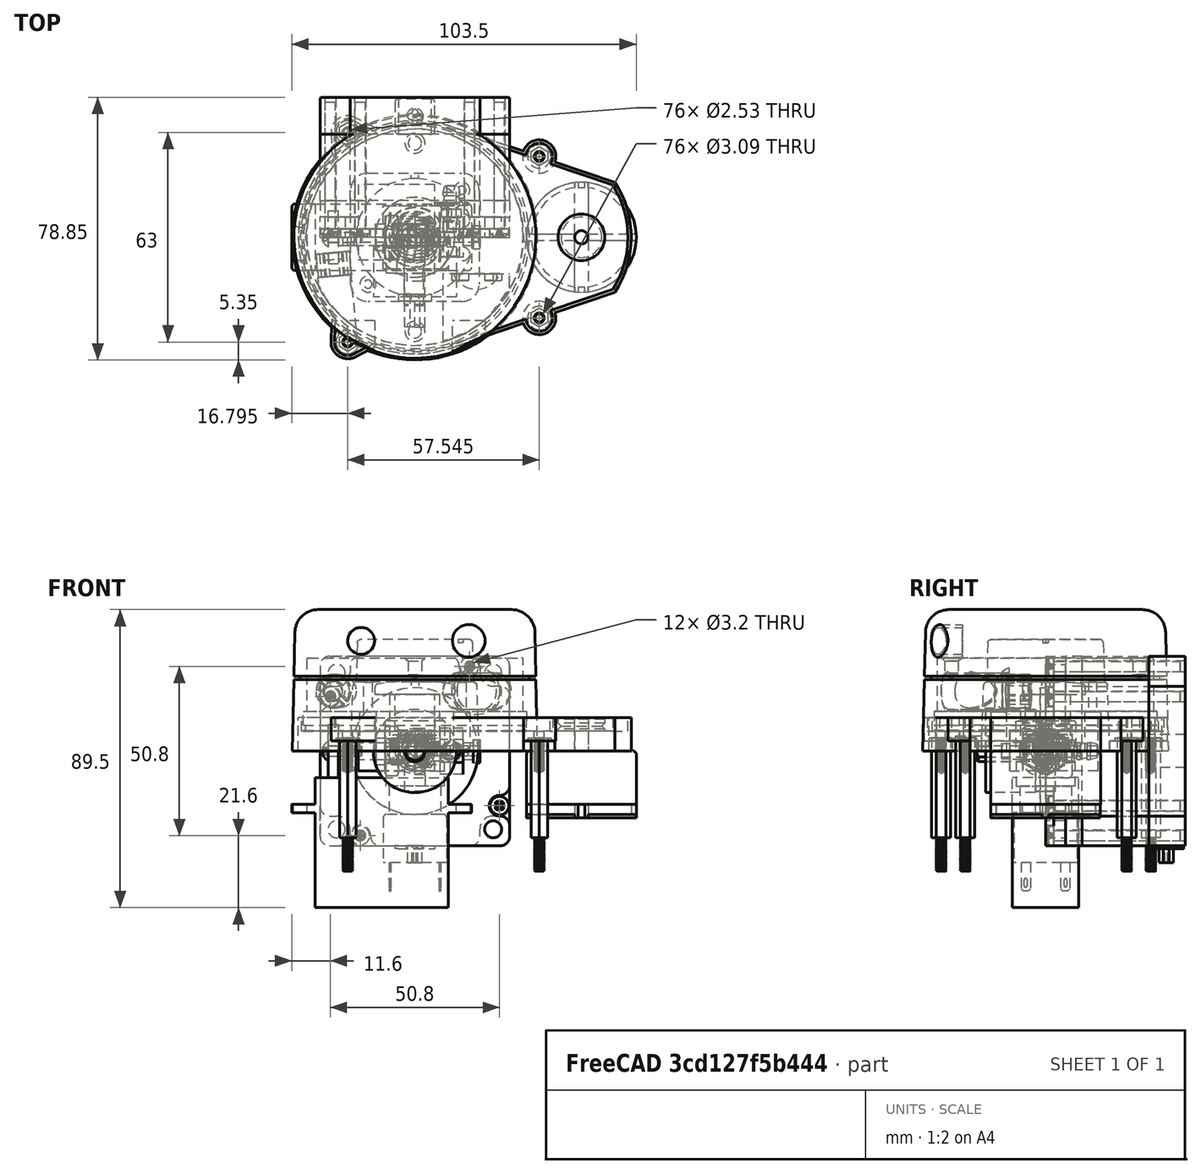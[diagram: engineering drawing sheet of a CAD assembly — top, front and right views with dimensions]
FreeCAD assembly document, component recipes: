
FREECAD ASSEMBLY — COMPONENT RECIPES ("generic-hardware")

This assembly document has 24 components, labeled P0..P23 below (a component is one placed body or linked part). 22 of them carry a construction recipe — the FreeCAD feature program that regenerates the part from scratch, quoted from this document or its linked companion documents; the rest are supplied as boundary geometry only. No exploded tour is included for this assembly.
NOTE — document 2 of 2 of this assembly tour. The two overview renders and the header above are repeated from document 1; the component sections below continue where the previous document stopped.
COMPONENT P19 — recipe-attached ("BAU-2195813", modeled in this document).
Construction recipe (the document's own serialized feature program — sketch geometry with constraints, then the solid features built on it; lengths are millimeters unless a unit is written):

FEATURE [Sketcher::SketchObject] Sketch171
  ArcFitTolerance = 0
  AttachmentSupport = -> [XY_Plane102]
  ExternalBSplineMaxDegree = 0
  ExternalBSplineTolerance = 0
  FixShape = 1
  FullyConstrained = true
  InternalTolerance = 1e-06
  InvalidShape = false
  MakeInternals = false
  MapMode = 5
  Support = -> [XY_Plane102]
  TreeRank = 111
  ValidateShape = false
  sketch-geometry (1):
    g0: Circle CenterX=0 CenterY=0 CenterZ=0 NormalX=0 NormalY=0 NormalZ=1 AngleXU=0 Radius=9
  constraints (2):
    c: Coincident(g0,g-1)
    c: Diameter(g0) = 18
FEATURE [PartDesign::Pad] Pad073
  AddSubType = 0
  AlongSketchNormal = false
  AutoTaperInnerAngle = false
  CheckUpToFaceLimits = true
  ClaimChildren = false
  Direction = (0,0,1)
  Fit = 0
  FitJoin = 0
  FixShape = 1
  InnerFit = 0
  InnerFitJoin = 0
  InvalidShape = false
  Length = 9
  Length2 = 100
  Linearize = true
  NewSolid = false
  Profile = -> Sketch171
  Refine = true
  Suppress = false
  TaperInnerAngle = 0
  TaperInnerAngleRev = 0
  TreeRank = 112
  Type = 0
  ValidateShape = false
  _ProfileBasedVersion = 1
FEATURE [PartDesign::Fillet] Fillet041
  AddSubType = 0
  Base = -> Pad073 [Edge3]
  BaseFeature = -> Pad073
  FixShape = 1
  InvalidShape = false
  NewSolid = false
  Radius = 0.4
  Refine = true
  SupportTransform = false
  Suppress = false
  TreeRank = 113
  UseAllEdges = false
  ValidateShape = false
FEATURE [Sketcher::SketchObject] Sketch172
  ArcFitTolerance = 0
  AttachmentSupport = -> [XZ_Plane102]
  ExternalBSplineMaxDegree = 0
  ExternalBSplineTolerance = 0
  FixShape = 1
  FullyConstrained = true
  InternalTolerance = 1e-06
  InvalidShape = false
  MakeInternals = false
  MapMode = 5
  Placement = pos=(0,0,0) rot=(1,0,0;1.5708rad)
  Support = -> [XZ_Plane102]
  TreeRank = 114
  ValidateShape = false
  sketch-geometry (8):
    g0: LineSegment StartX=0 StartY=-2.075e-13 StartZ=0 EndX=7.75 EndY=-2.075e-13 EndZ=0
    g1: LineSegment StartX=7.75 StartY=-2.075e-13 StartZ=0 EndX=7.75 EndY=-3 EndZ=0
    g2: LineSegment StartX=7.75 StartY=-3 StartZ=0 EndX=8.8 EndY=-3 EndZ=0
    g3: LineSegment StartX=8.8 StartY=-3 StartZ=0 EndX=8.8 EndY=-10.5 EndZ=0
    g4: LineSegment StartX=8.8 StartY=-10.5 StartZ=0 EndX=7.75 EndY=-10.5 EndZ=0
    g5: LineSegment StartX=7.75 StartY=-10.5 StartZ=0 EndX=7.75 EndY=-19 EndZ=0
    g6: LineSegment StartX=7.75 StartY=-19 StartZ=0 EndX=0 EndY=-19 EndZ=0
    g7: LineSegment StartX=0 StartY=-19 StartZ=0 EndX=0 EndY=-2.061e-13 EndZ=0
  constraints (23):
    c: Coincident(g-1,g0)
    c: Horizontal(g0)
    c: Coincident(g0,g1)
    c: Vertical(g1)
    c: Coincident(g1,g2)
    c: Horizontal(g2)
    c: Coincident(g2,g3)
    c: Vertical(g3)
    c: Coincident(g3,g4)
    c: Coincident(g4,g5)
    c: Vertical(g5)
    c: Coincident(g5,g6)
    c: PointOnObject(g6,g-2)
    c: Horizontal(g6)
    c: Coincident(g6,g7)
    c: Coincident(g7,g0)
    c: DistanceY(g1,g1) = 3
    c: DistanceX(g2) = 8.8
    c: DistanceX(g1) = 7.75
    c: PointOnObject(g5,g1)
    c: DistanceY(g3,g3) = 7.5
    c: Horizontal(g4)
    c: DistanceY(g7,g7) = 19
FEATURE [PartDesign::Revolution] Revolution014
  AddSubType = 0
  Angle = 360
  Axis = (0,2e-16,1)
  Base = (0,0,0)
  BaseFeature = -> Fillet041
  ClaimChildren = false
  Fit = 0
  FitJoin = 0
  FixShape = 1
  InnerFit = 0
  InnerFitJoin = 0
  InvalidShape = false
  Linearize = true
  NewSolid = false
  Profile = -> Sketch172
  ReferenceAxis = -> Sketch172 [V_Axis]
  Refine = true
  Reversed = true
  Suppress = false
  TreeRank = 115
  ValidateShape = false
  _ProfileBasedVersion = 1
FEATURE [PartDesign::Body] Body082  label="MainBody"
  AutoGroupSolids = false
  ClaimAllChildren = false
  ExportMode = 0
  FixShape = 1
  Group = -> [Sketch171,Pad073,Fillet041,Sketch172,Revolution014]
  InvalidShape = false
  Origin = -> Origin169
  SingleSolid = true
  Tip = -> Revolution014
  TreeRank = 110
  ValidateShape = false
  _ExportChildren = -> [Pad073,Fillet041,Revolution014]
  _GroupVersion = 1
FEATURE [Part::SubShapeBinder] Import002  label="Import002(Revolution014)"
  BindCopyOnChange = 0
  BindMode = 0
  ClaimChildren = false
  Context = -> Part036 [Body083.Import002.]
  EdgeTolerance = 1e-06
  FillStyle = 0
  FixShape = 1
  Fuse = false
  InvalidShape = false
  MakeFace = false
  MergeEdges = true
  OffsetFill = false
  OffsetIntersection = false
  OffsetJoinType = 0
  OffsetOpenResult = false
  Outline = false
  PartialLoad = false
  Relative = true
  SplitEdges = false
  Support = -> [Body082[Revolution014.]]
  TightBound = false
  TreeRank = 127
  ValidateShape = false
  _Version = 8
FEATURE [Sketcher::SketchObject] Sketch173
  ArcFitTolerance = 0
  AttachmentSupport = -> [Import002]
  ExternalBSplineMaxDegree = 0
  ExternalBSplineTolerance = 0
  FixShape = 1
  FullyConstrained = true
  InternalTolerance = 1e-06
  InvalidShape = false
  MakeInternals = false
  MapMode = 5
  Placement = pos=(0,-4.2e-15,-19) rot=(1,0,0;3.14159rad)
  Support = -> [Import002]
  TreeRank = 126
  ValidateShape = false
  sketch-geometry (5):
    g0: LineSegment StartX=9.5 StartY=9.5 StartZ=0 EndX=-9.5 EndY=9.5 EndZ=0
    g1: LineSegment StartX=-9.5 StartY=9.5 StartZ=0 EndX=-9.5 EndY=-9.5 EndZ=0
    g2: LineSegment StartX=-9.5 StartY=-9.5 StartZ=0 EndX=9.5 EndY=-9.5 EndZ=0
    g3: LineSegment StartX=9.5 StartY=-9.5 StartZ=0 EndX=9.5 EndY=9.5 EndZ=0
    g4: Circle [constr] CenterX=-1.2948e-12 CenterY=-4.7939e-12 CenterZ=0 NormalX=0 NormalY=0 NormalZ=1 AngleXU=0 Radius=13.435
  constraints (14):
    c: Coincident(g0,g1)
    c: Coincident(g1,g2)
    c: Coincident(g2,g3)
    c: Coincident(g3,g0)
    c: Equal(g0,g1)
    c: Equal(g0,g2)
    c: Equal(g0,g3)
    c: PointOnObject(g0,g4)
    c: PointOnObject(g1,g4)
    c: PointOnObject(g2,g4)
    c: PointOnObject(g3,g4)
    c: Coincident(g4,g-1)
    c: Horizontal(g0)
    c: DistanceX(g0,g0) = 19
FEATURE [PartDesign::Pad] Pad074
  AddSubType = 0
  AlongSketchNormal = false
  AutoTaperInnerAngle = false
  CheckUpToFaceLimits = true
  ClaimChildren = false
  Direction = (0,-2e-16,-1)
  Fit = 0
  FitJoin = 0
  FixShape = 1
  InnerFit = 0
  InnerFitJoin = 0
  InvalidShape = false
  Length = 14.5
  Length2 = 100
  Linearize = true
  NewSolid = false
  Profile = -> Sketch173
  Refine = true
  Suppress = false
  TaperInnerAngle = 0
  TaperInnerAngleRev = 0
  TreeRank = 128
  Type = 0
  ValidateShape = false
  _ProfileBasedVersion = 1
FEATURE [PartDesign::Fillet] Fillet042
  AddSubType = 0
  Base = -> Pad074 [Edge11,Edge6]
  BaseFeature = -> Pad074
  FixShape = 1
  InvalidShape = false
  NewSolid = false
  Radius = 1
  Refine = true
  SupportTransform = false
  Suppress = false
  TreeRank = 129
  UseAllEdges = false
  ValidateShape = false
FEATURE [PartDesign::Body] Body083  label="ElectronicBody"
  AutoGroupSolids = false
  ClaimAllChildren = false
  ExportMode = 0
  FixShape = 1
  Group = -> [Sketch173,Import002,Pad074,Fillet042]
  InvalidShape = false
  Origin = -> Origin170
  SingleSolid = true
  Tip = -> Fillet042
  TreeRank = 125
  ValidateShape = false
  _ExportChildren = -> [Import002,Pad074,Fillet042]
  _GroupVersion = 1
FEATURE [Part::SubShapeBinder] Import003  label="Import003(Fillet042)"
  BindCopyOnChange = 0
  BindMode = 0
  ClaimChildren = false
  Context = -> Part036 [Body084.Import003.]
  EdgeTolerance = 1e-06
  FillStyle = 0
  FixShape = 1
  Fuse = false
  InvalidShape = false
  MakeFace = false
  MergeEdges = true
  OffsetFill = false
  OffsetIntersection = false
  OffsetJoinType = 0
  OffsetOpenResult = false
  Outline = false
  PartialLoad = false
  Relative = true
  SplitEdges = false
  Support = -> [Body083[Fillet042.]]
  TightBound = false
  TreeRank = 141
  ValidateShape = false
  _Version = 8
FEATURE [Sketcher::SketchObject] Sketch174
  ArcFitTolerance = 0
  AttachmentSupport = -> [Import003]
  ExternalBSplineMaxDegree = 0
  ExternalBSplineTolerance = 0
  FixShape = 1
  FullyConstrained = true
  InternalTolerance = 1e-06
  InvalidShape = false
  MakeInternals = false
  MapMode = 5
  Placement = pos=(0,-1.25e-14,-33.5) rot=(1,0,0;3.14159rad)
  Support = -> [Import003]
  TreeRank = 140
  ValidateShape = false
  sketch-geometry (16):
    g0: LineSegment StartX=-7.75 StartY=7.3 StartZ=0 EndX=-7.25 EndY=7.3 EndZ=0
    g1: LineSegment StartX=-7.25 StartY=7.3 StartZ=0 EndX=-7.25 EndY=4.5 EndZ=0
    g2: LineSegment StartX=-7.25 StartY=4.5 StartZ=0 EndX=-7.75 EndY=4.5 EndZ=0
    g3: LineSegment StartX=-7.75 StartY=4.5 StartZ=0 EndX=-7.75 EndY=7.3 EndZ=0
    g4: LineSegment StartX=7.25 StartY=7.3 StartZ=0 EndX=7.75 EndY=7.3 EndZ=0
    g5: LineSegment StartX=7.75 StartY=7.3 StartZ=0 EndX=7.75 EndY=4.5 EndZ=0
    g6: LineSegment StartX=7.75 StartY=4.5 StartZ=0 EndX=7.25 EndY=4.5 EndZ=0
    g7: LineSegment StartX=7.25 StartY=4.5 StartZ=0 EndX=7.25 EndY=7.3 EndZ=0
    g8: LineSegment StartX=7.25 StartY=-4.5 StartZ=0 EndX=7.75 EndY=-4.5 EndZ=0
    g9: LineSegment StartX=7.75 StartY=-4.5 StartZ=0 EndX=7.75 EndY=-7.3 EndZ=0
    g10: LineSegment StartX=7.75 StartY=-7.3 StartZ=0 EndX=7.25 EndY=-7.3 EndZ=0
    g11: LineSegment StartX=7.25 StartY=-7.3 StartZ=0 EndX=7.25 EndY=-4.5 EndZ=0
    g12: LineSegment StartX=-7.75 StartY=-4.5 StartZ=0 EndX=-7.25 EndY=-4.5 EndZ=0
    g13: LineSegment StartX=-7.25 StartY=-4.5 StartZ=0 EndX=-7.25 EndY=-7.3 EndZ=0
    g14: LineSegment StartX=-7.25 StartY=-7.3 StartZ=0 EndX=-7.75 EndY=-7.3 EndZ=0
    g15: LineSegment StartX=-7.75 StartY=-7.3 StartZ=0 EndX=-7.75 EndY=-4.5 EndZ=0
  constraints (46):
    c: Coincident(g0,g1)
    c: Coincident(g1,g2)
    c: Coincident(g2,g3)
    c: Coincident(g3,g0)
    c: Horizontal(g0)
    c: Horizontal(g2)
    c: Vertical(g1)
    c: Vertical(g3)
    c: DistanceX(g1,g-1) = 7.25
    c: DistanceX(g0,g0) = 0.5
    c: DistanceY(g3,g3) = 2.8
    c: DistanceY(g2) = 4.5
    c: Coincident(g4,g5)
    c: Coincident(g5,g6)
    c: Coincident(g6,g7)
    c: Coincident(g7,g4)
    c: Horizontal(g4)
    c: Horizontal(g6)
    c: Vertical(g5)
    c: Vertical(g7)
    c: Coincident(g8,g9)
    c: Coincident(g9,g10)
    c: Coincident(g10,g11)
    c: Coincident(g11,g8)
    c: Horizontal(g8)
    c: Horizontal(g10)
    c: Vertical(g9)
    c: Vertical(g11)
    c: Coincident(g12,g13)
    c: Coincident(g13,g14)
    c: Coincident(g14,g15)
    c: Coincident(g15,g12)
    c: Horizontal(g12)
    c: Horizontal(g14)
    c: Vertical(g13)
    c: Vertical(g15)
    c: Equal(g12,g8)
    c: Equal(g8,g6)
    c: Equal(g6,g2)
    c: Equal(g1,g7)
    c: Equal(g7,g11)
    c: Equal(g11,g13)
    c: Horizontal(g13,g10)
    c: Vertical(g8,g5)
    c: Symmetric(g0,g4,g-2)
    c: Symmetric(g12,g1,g-1)
FEATURE [PartDesign::Pad] Pad075
  AddSubType = 0
  AlongSketchNormal = false
  AutoTaperInnerAngle = false
  CheckUpToFaceLimits = true
  ClaimChildren = false
  Direction = (0,-4e-16,-1)
  Fit = 0
  FitJoin = 0
  FixShape = 1
  InnerFit = 0
  InnerFitJoin = 0
  InvalidShape = false
  Length = 8.5
  Length2 = 100
  Linearize = true
  NewSolid = false
  Profile = -> Sketch174
  Refine = true
  Suppress = false
  TaperInnerAngle = 0
  TaperInnerAngleRev = 0
  TreeRank = 142
  Type = 0
  ValidateShape = false
  _ProfileBasedVersion = 1
FEATURE [PartDesign::Chamfer] Chamfer045
  AddSubType = 0
  Angle = 45
  Base = -> Pad075 [Edge46,Edge40,Edge34,Edge28,Edge16,Edge22,Edge10,Edge4]
  BaseFeature = -> Pad075
  ChamferType = 0
  FixShape = 1
  FlipDirection = false
  InvalidShape = false
  NewSolid = false
  Refine = true
  Size = 0.6
  Size2 = 1
  SupportTransform = false
  Suppress = false
  TreeRank = 143
  UseAllEdges = false
  ValidateShape = false
FEATURE [Sketcher::SketchObject] Sketch175
  ArcFitTolerance = 0
  AttachmentSupport = -> [YZ_Plane104]
  ExternalBSplineMaxDegree = 0
  ExternalBSplineTolerance = 0
  FixShape = 1
  FullyConstrained = false
  InternalTolerance = 1e-06
  InvalidShape = false
  MakeInternals = false
  MapMode = 5
  Placement = pos=(0,0,0) rot=(0.57735,0.57735,0.57735;2.0944rad)
  Support = -> [YZ_Plane104]
  TreeRank = 144
  ValidateShape = false
  sketch-geometry (8):
    g0: ArcOfCircle CenterX=-6 CenterY=-38.7066 CenterZ=0 NormalX=0 NormalY=0 NormalZ=1 AngleXU=0 Radius=0.456793 StartAngle=1.3e-15 EndAngle=3.14159
    g1: ArcOfCircle CenterX=-6 CenterY=-40.4194 CenterZ=0 NormalX=0 NormalY=0 NormalZ=1 AngleXU=0 Radius=0.456793 StartAngle=3.14159 EndAngle=6.28319
    g2: LineSegment StartX=-6.45679 StartY=-38.7066 StartZ=0 EndX=-6.45679 EndY=-40.4194 EndZ=0
    g3: LineSegment StartX=-5.54321 StartY=-40.4194 StartZ=0 EndX=-5.54321 EndY=-38.7066 EndZ=0
    g4: ArcOfCircle CenterX=6 CenterY=-38.7066 CenterZ=0 NormalX=0 NormalY=0 NormalZ=1 AngleXU=0 Radius=0.417287 StartAngle=-5.3e-15 EndAngle=3.14159
    g5: ArcOfCircle CenterX=6 CenterY=-40.4194 CenterZ=0 NormalX=0 NormalY=0 NormalZ=1 AngleXU=0 Radius=0.417287 StartAngle=3.14159 EndAngle=6.28319
    g6: LineSegment StartX=5.58271 StartY=-38.7066 StartZ=0 EndX=5.58271 EndY=-40.4194 EndZ=0
    g7: LineSegment StartX=6.41729 StartY=-40.4194 StartZ=0 EndX=6.41729 EndY=-38.7066 EndZ=0
  constraints (14):
    c: Tangent(g0,g2) = -1.5708
    c: Tangent(g2,g1) = -1.5708
    c: Tangent(g1,g3) = -1.5708
    c: Tangent(g3,g0) = -1.5708
    c: Equal(g0,g1)
    c: Tangent(g4,g6) = -1.5708
    c: Tangent(g6,g5) = -1.5708
    c: Tangent(g5,g7) = -1.5708
    c: Tangent(g7,g4) = -1.5708
    c: Equal(g4,g5)
    c: Symmetric(g4,g0,g-2)
    c: Symmetric(g5,g1,g-2)
    c: Vertical(g1,g0)
    c: DistanceX(g0) = -6
FEATURE [PartDesign::Pocket] Pocket054
  AddSubType = 1
  AutoTaperInnerAngle = false
  BaseFeature = -> Chamfer045
  CheckUpToFaceLimits = true
  ClaimChildren = false
  Direction = (1,1,1)
  Fit = 0
  FitJoin = 0
  FixShape = 1
  InnerFit = 0
  InnerFitJoin = 0
  InvalidShape = false
  Length = 5
  Length2 = 100
  Linearize = true
  Midplane = true
  NewSolid = false
  Profile = -> Sketch175
  Refine = true
  Suppress = false
  TaperInnerAngle = 0
  TaperInnerAngleRev = 0
  TreeRank = 145
  Type = 1
  ValidateShape = false
  _ProfileBasedVersion = 1
  _Version = 1
FEATURE [PartDesign::Body] Body084  label="ElectronicPins"
  AutoGroupSolids = false
  ClaimAllChildren = false
  ExportMode = 0
  FixShape = 1
  Group = -> [Sketch174,Import003,Pad075,Chamfer045,Sketch175,Pocket054]
  InvalidShape = false
  Origin = -> Origin171
  Tip = -> Pocket054
  TreeRank = 139
  ValidateShape = false
  _ExportChildren = -> [Import003,Pad075,Chamfer045,Pocket054]
  _GroupVersion = 1
FEATURE [Sketcher::SketchObject] Sketch176
  ArcFitTolerance = 0
  AttachmentSupport = -> [YZ_Plane105]
  ExternalBSplineMaxDegree = 0
  ExternalBSplineTolerance = 0
  FixShape = 1
  FullyConstrained = true
  InternalTolerance = 1e-06
  InvalidShape = false
  MakeInternals = false
  MapMode = 5
  Placement = pos=(0,0,0) rot=(0.57735,0.57735,0.57735;2.0944rad)
  Support = -> [YZ_Plane105]
  TreeRank = 156
  ValidateShape = false
  sketch-geometry (12):
    g0: LineSegment StartX=-7.5 StartY=0 StartZ=0 EndX=-7.5 EndY=17 EndZ=0
    g1: LineSegment StartX=-7.5 StartY=17 StartZ=0 EndX=-12 EndY=17 EndZ=0
    g2: LineSegment StartX=-12 StartY=17 StartZ=0 EndX=-12 EndY=20 EndZ=0
    g3: LineSegment [constr] StartX=-7.5 StartY=0 StartZ=0 EndX=7.5 EndY=0 EndZ=0
    g4: LineSegment [constr] StartX=7.5 StartY=0 StartZ=0 EndX=7.5 EndY=17 EndZ=0
    g5: LineSegment [constr] StartX=7.5 StartY=17 StartZ=0 EndX=12 EndY=17 EndZ=0
    g6: LineSegment [constr] StartX=12 StartY=17 StartZ=0 EndX=12 EndY=20 EndZ=0
    g7: ArcOfCircle [constr] CenterX=-1.51e-14 CenterY=-51.5 CenterZ=0 NormalX=0 NormalY=0 NormalZ=1 AngleXU=0 Radius=72.5 StartAngle=1.40451 EndAngle=1.73708
    g8: GeomPoint [constr] X=4.5e-15 Y=21 Z=0
    g9: LineSegment StartX=0 StartY=0 StartZ=0 EndX=4.5e-15 EndY=21 EndZ=0
    g10: LineSegment StartX=-7.5 StartY=0 StartZ=0 EndX=0 EndY=0 EndZ=0
    g11: ArcOfCircle CenterX=-1.51e-14 CenterY=-51.5 CenterZ=0 NormalX=0 NormalY=0 NormalZ=1 AngleXU=0 Radius=72.5 StartAngle=1.5708 EndAngle=1.73708
  constraints (31):
    c: PointOnObject(g0,g-1)
    c: Vertical(g0)
    c: Coincident(g0,g1)
    c: Horizontal(g1)
    c: Coincident(g1,g2)
    c: Coincident(g0,g3)
    c: Coincident(g3,g4)
    c: Vertical(g4)
    c: Coincident(g4,g5)
    c: Horizontal(g5)
    c: Coincident(g5,g6)
    c: Vertical(g6)
    c: Vertical(g2)
    c: Equal(g6,g2)
    c: Symmetric(g0,g3,g-1)
    c: Symmetric(g6,g2,g-2)
    c: DistanceX(g0,g4) = 15
    c: DistanceY(g4) = 17
    c: DistanceY(g2,g2) = 3
    c: DistanceX(g1,g5) = 24
    c: Coincident(g7,g2)
    c: Coincident(g7,g6)
    c: PointOnObject(g8,g-2)
    c: Coincident(g9,g-1)
    c: Coincident(g9,g8)
    c: Coincident(g10,g0)
    c: Coincident(g10,g9)
    c: Coincident(g11,g7)
    c: Coincident(g11,g9)
    c: Coincident(g11,g2)
    c: DistanceY(g9) = 21
FEATURE [PartDesign::Revolution] Revolution015
  AddSubType = 0
  Angle = 360
  Axis = (-2e-16,3e-16,1)
  Base = (0,0,0)
  ClaimChildren = false
  Fit = 0
  FitJoin = 0
  FixShape = 1
  InnerFit = 0
  InnerFitJoin = 0
  InvalidShape = false
  Linearize = true
  NewSolid = false
  Placement = pos=(0,0,0) rot=(0.57735,0.57735,0.57735;2.0944rad)
  Profile = -> Sketch176
  ReferenceAxis = -> Sketch176 [V_Axis]
  Refine = true
  Suppress = false
  TreeRank = 157
  ValidateShape = false
  _ProfileBasedVersion = 1
FEATURE [PartDesign::Fillet] Fillet043
  AddSubType = 0
  Base = -> Revolution015 [Edge5]
  BaseFeature = -> Revolution015
  FixShape = 1
  InvalidShape = false
  NewSolid = false
  Placement = pos=(0,0,0) rot=(0.57735,0.57735,0.57735;2.0944rad)
  Radius = 1
  Refine = true
  SupportTransform = false
  Suppress = false
  TreeRank = 158
  UseAllEdges = false
  ValidateShape = false
FEATURE [PartDesign::Body] Body085  label="ButtonCaps"
  AutoGroupSolids = false
  ClaimAllChildren = false
  ExportMode = 0
  FixShape = 1
  Group = -> [Sketch176,Revolution015,Fillet043]
  InvalidShape = false
  Origin = -> Origin172
  SingleSolid = true
  Tip = -> Fillet043
  TreeRank = 155
  ValidateShape = false
  _ExportChildren = -> [Revolution015,Fillet043]
  _GroupVersion = 1
COMPONENT P20 — geometry summary ("ConnecteurPneu-Ressort"; no construction recipe available for this part):
  bounding box: 47.1 x 23.5 x 16.0 mm
  tessellated surface: 18,782 triangles
  volume: 3419 mm^3 (19% of its bounding box)
  symmetry: mirror-symmetric across its z mid-plane
COMPONENT P21 — recipe-attached ("623ZZ", modeled in this document).
Construction recipe (the document's own serialized feature program — sketch geometry with constraints, then the solid features built on it; lengths are millimeters unless a unit is written):

FEATURE [Sketcher::SketchObject] Sketch202
  ArcFitTolerance = 1e-06
  AttachmentSupport = -> [XY_Plane117]
  ExternalBSplineMaxDegree = 5
  ExternalBSplineTolerance = 0.0001
  FixShape = 1
  FullyConstrained = true
  InternalTolerance = 1e-06
  InvalidShape = false
  MakeInternals = false
  MapMode = 5
  Support = -> [XY_Plane117]
  TreeRank = 345
  ValidateShape = false
  sketch-geometry (12):
    g0: LineSegment StartX=0 StartY=1.5 StartZ=0 EndX=4 EndY=1.5 EndZ=0
    g1: LineSegment StartX=4 StartY=1.5 StartZ=0 EndX=4 EndY=2.5 EndZ=0
    g2: LineSegment StartX=4 StartY=2.5 StartZ=0 EndX=3.5 EndY=2.5 EndZ=0
    g3: LineSegment StartX=3.5 StartY=2.5 StartZ=0 EndX=3.5 EndY=4 EndZ=0
    g4: LineSegment StartX=3.5 StartY=4 StartZ=0 EndX=4 EndY=4 EndZ=0
    g5: LineSegment StartX=4 StartY=4 StartZ=0 EndX=4 EndY=5 EndZ=0
    g6: LineSegment StartX=4 StartY=5 StartZ=0 EndX=0 EndY=5 EndZ=0
    g7: LineSegment StartX=0 StartY=5 StartZ=0 EndX=0 EndY=4 EndZ=0
    g8: LineSegment StartX=0 StartY=4 StartZ=0 EndX=0.5 EndY=4 EndZ=0
    g9: LineSegment StartX=0.5 StartY=4 StartZ=0 EndX=0.5 EndY=2.5 EndZ=0
    g10: LineSegment StartX=0.5 StartY=2.5 StartZ=0 EndX=0 EndY=2.5 EndZ=0
    g11: LineSegment StartX=0 StartY=2.5 StartZ=0 EndX=0 EndY=1.5 EndZ=0
  constraints (36):
    c: PointOnObject(g0,g-2)
    c: Horizontal(g0)
    c: Coincident(g1,g0)
    c: Vertical(g1)
    c: Coincident(g1,g2)
    c: Horizontal(g2)
    c: Coincident(g2,g3)
    c: Vertical(g3)
    c: Coincident(g3,g4)
    c: Horizontal(g4)
    c: Coincident(g4,g5)
    c: Vertical(g5)
    c: Coincident(g5,g6)
    c: PointOnObject(g6,g-2)
    c: Horizontal(g6)
    c: Coincident(g6,g7)
    c: PointOnObject(g7,g-2)
    c: Coincident(g7,g8)
    c: Horizontal(g8)
    c: Coincident(g8,g9)
    c: Vertical(g9)
    c: Coincident(g9,g10)
    c: PointOnObject(g10,g-2)
    c: Horizontal(g10)
    c: Coincident(g10,g11)
    c: Coincident(g11,g0)
    c: Equal(g4,g8)
    c: Equal(g10,g2)
    c: DistanceY(g-1,g0) = 1.5
    c: PointOnObject(g9,g2)
    c: PointOnObject(g8,g4)
    c: DistanceY(g-1,g6) = 5
    c: DistanceY(g-1,g10) = 2.5
    c: DistanceY(g-1,g7) = 4
    c: DistanceX(g6,g6) = 4
    c: DistanceX(g8,g3) = 3
FEATURE [PartDesign::Revolution] Revolution018
  AddSubType = 0
  Angle = 360
  Axis = (1,0,0)
  Base = (0,0,0)
  ClaimChildren = false
  Fit = 0
  FitJoin = 0
  FixShape = 1
  InnerFit = 0
  InnerFitJoin = 0
  InvalidShape = false
  Linearize = true
  NewSolid = false
  Profile = -> Sketch202
  ReferenceAxis = -> Sketch202 [H_Axis]
  Refine = true
  Suppress = false
  TreeRank = 346
  ValidateShape = false
  _ProfileBasedVersion = 1
FEATURE [PartDesign::Body] Body097
  AutoGroupSolids = false
  ClaimAllChildren = false
  ExportMode = 0
  FixShape = 1
  Group = -> [Sketch202,Revolution018]
  InvalidShape = false
  Origin = -> Origin188
  SingleSolid = true
  Tip = -> Revolution018
  TreeRank = 344
  ValidateShape = false
  _ExportChildren = -> [Revolution018]
  _GroupVersion = 1
FEATURE [Sketcher::SketchObject] Sketch203
  ArcFitTolerance = 1e-06
  AttachmentSupport = -> [XY_Plane118]
  ExternalBSplineMaxDegree = 5
  ExternalBSplineTolerance = 0.0001
  FixShape = 1
  FullyConstrained = true
  InternalTolerance = 1e-06
  InvalidShape = false
  MakeInternals = false
  MapMode = 5
  Support = -> [XY_Plane118]
  TreeRank = 357
  ValidateShape = false
  sketch-geometry (4):
    g0: LineSegment StartX=0.1 StartY=4 StartZ=0 EndX=3.9 EndY=4 EndZ=0
    g1: LineSegment StartX=3.9 StartY=4 StartZ=0 EndX=3.9 EndY=2.5 EndZ=0
    g2: LineSegment StartX=3.9 StartY=2.5 StartZ=0 EndX=0.1 EndY=2.5 EndZ=0
    g3: LineSegment StartX=0.1 StartY=2.5 StartZ=0 EndX=0.1 EndY=4 EndZ=0
  constraints (12):
    c: Coincident(g0,g1)
    c: Coincident(g1,g2)
    c: Coincident(g2,g3)
    c: Coincident(g3,g0)
    c: Horizontal(g0)
    c: Horizontal(g2)
    c: Vertical(g1)
    c: Vertical(g3)
    c: DistanceY(g-1,g2) = 2.5
    c: DistanceY(g-1,g0) = 4
    c: DistanceX(g0,g0) = 3.8
    c: DistanceX(g-1,g2) = 0.1
FEATURE [PartDesign::Revolution] Revolution019
  AddSubType = 0
  Angle = 360
  Axis = (1,0,0)
  Base = (0,0,0)
  ClaimChildren = false
  Fit = 0
  FitJoin = 0
  FixShape = 1
  InnerFit = 0
  InnerFitJoin = 0
  InvalidShape = false
  Linearize = true
  NewSolid = false
  Profile = -> Sketch203
  ReferenceAxis = -> Sketch203 [H_Axis]
  Refine = true
  Suppress = false
  TreeRank = 358
  ValidateShape = false
  _ProfileBasedVersion = 1
FEATURE [PartDesign::Body] Body098
  AutoGroupSolids = false
  ClaimAllChildren = false
  ExportMode = 0
  FixShape = 1
  Group = -> [Sketch203,Revolution019]
  InvalidShape = false
  Origin = -> Origin189
  SingleSolid = true
  Tip = -> Revolution019
  TreeRank = 356
  ValidateShape = false
  _ExportChildren = -> [Revolution019]
  _GroupVersion = 1
COMPONENT P22 — recipe-attached ("V623ZZ", modeled in this document).
Construction recipe (the document's own serialized feature program — sketch geometry with constraints, then the solid features built on it; lengths are millimeters unless a unit is written):

FEATURE [Sketcher::SketchObject] Sketch204
  ArcFitTolerance = 1e-06
  AttachmentSupport = -> [XY_Plane121]
  ExternalBSplineMaxDegree = 5
  ExternalBSplineTolerance = 0.0001
  FixShape = 1
  FullyConstrained = true
  InternalTolerance = 1e-06
  InvalidShape = false
  MakeInternals = false
  MapMode = 5
  Support = -> [XY_Plane121]
  TreeRank = 396
  ValidateShape = false
  sketch-geometry (7):
    g0: LineSegment StartX=4 StartY=0 StartZ=0 EndX=4 EndY=4 EndZ=0
    g1: LineSegment StartX=4 StartY=4 StartZ=0 EndX=6 EndY=4 EndZ=0
    g2: LineSegment StartX=6 StartY=4 StartZ=0 EndX=6 EndY=3.25 EndZ=0
    g3: LineSegment StartX=6 StartY=3.25 StartZ=0 EndX=4.85 EndY=2 EndZ=0
    g4: LineSegment StartX=4.85 StartY=2 StartZ=0 EndX=6 EndY=0.75 EndZ=0
    g5: LineSegment StartX=6 StartY=0.75 StartZ=0 EndX=6 EndY=0 EndZ=0
    g6: LineSegment StartX=6 StartY=0 StartZ=0 EndX=4 EndY=0 EndZ=0
  constraints (21):
    c: PointOnObject(g0,g-1)
    c: Vertical(g0)
    c: Coincident(g0,g1)
    c: Horizontal(g1)
    c: Coincident(g1,g2)
    c: Vertical(g2)
    c: Coincident(g2,g3)
    c: Coincident(g3,g4)
    c: Coincident(g4,g5)
    c: PointOnObject(g5,g-1)
    c: Vertical(g5)
    c: Coincident(g5,g6)
    c: Coincident(g6,g0)
    c: DistanceX(g-1,g0) = 4
    c: Equal(g3,g4)
    c: Equal(g1,g6)
    c: Equal(g5,g2)
    c: DistanceX(g-1,g5) = 6
    c: DistanceX(g-1,g3) = 4.85
    c: DistanceY(g0,g0) = 4
    c: DistanceY(g4,g2) = 2.5
FEATURE [PartDesign::Revolution] Revolution020
  AddSubType = 0
  Angle = 360
  Axis = (0,1,0)
  Base = (0,0,0)
  ClaimChildren = false
  Fit = 0
  FitJoin = 0
  FixShape = 1
  InnerFit = 0
  InnerFitJoin = 0
  InvalidShape = false
  Linearize = true
  NewSolid = false
  Profile = -> Sketch204
  ReferenceAxis = -> Sketch204 [V_Axis]
  Refine = true
  Reversed = true
  Suppress = false
  TreeRank = 397
  ValidateShape = false
  _ProfileBasedVersion = 1
FEATURE [PartDesign::Body] Body101  label="V623ZZ-extern"
  AutoGroupSolids = false
  ClaimAllChildren = false
  ExportMode = 0
  FixShape = 1
  Group = -> [Sketch204,Revolution020]
  InvalidShape = false
  Origin = -> Origin194
  SingleSolid = true
  Tip = -> Revolution020
  TreeRank = 395
  ValidateShape = false
  _ExportChildren = -> [Revolution020]
  _GroupVersion = 1
FEATURE [Sketcher::SketchObject] Sketch205
  ArcFitTolerance = 1e-06
  AttachmentSupport = -> [YZ_Plane120]
  ExternalBSplineMaxDegree = 5
  ExternalBSplineTolerance = 0.0001
  FixShape = 1
  FullyConstrained = true
  InternalTolerance = 1e-06
  InvalidShape = false
  MakeInternals = false
  MapMode = 5
  Placement = pos=(0,0,0) rot=(0.57735,0.57735,0.57735;2.0944rad)
  Support = -> [YZ_Plane120]
  TreeRank = 398
  ValidateShape = false
  sketch-geometry (8):
    g0: LineSegment StartX=0.2 StartY=4 StartZ=0 EndX=0.2 EndY=2.1 EndZ=0
    g1: LineSegment StartX=0.2 StartY=2.1 StartZ=0 EndX=0 EndY=2.1 EndZ=0
    g2: LineSegment StartX=0 StartY=2.1 StartZ=0 EndX=0 EndY=1.5 EndZ=0
    g3: LineSegment StartX=0 StartY=1.5 StartZ=0 EndX=4 EndY=1.5 EndZ=0
    g4: LineSegment StartX=4 StartY=1.5 StartZ=0 EndX=4 EndY=2.1 EndZ=0
    g5: LineSegment StartX=4 StartY=2.1 StartZ=0 EndX=3.8 EndY=2.1 EndZ=0
    g6: LineSegment StartX=3.8 StartY=2.1 StartZ=0 EndX=3.8 EndY=4 EndZ=0
    g7: LineSegment StartX=3.8 StartY=4 StartZ=0 EndX=0.2 EndY=4 EndZ=0
  constraints (24):
    c: Vertical(g0)
    c: Coincident(g0,g1)
    c: PointOnObject(g1,g-2)
    c: Horizontal(g1)
    c: Coincident(g1,g2)
    c: PointOnObject(g2,g-2)
    c: Coincident(g2,g3)
    c: Horizontal(g3)
    c: Coincident(g3,g4)
    c: Coincident(g4,g5)
    c: Horizontal(g5)
    c: Coincident(g5,g6)
    c: Vertical(g6)
    c: Coincident(g6,g7)
    c: Coincident(g7,g0)
    c: Horizontal(g7)
    c: DistanceY(g-1,g0) = 4
    c: Equal(g1,g5)
    c: Equal(g4,g2)
    c: DistanceX(g3,g3) = 4
    c: Vertical(g4)
    c: DistanceY(g-1,g2) = 1.5
    c: DistanceY(g2,g2) = 0.6
    c: DistanceX(g1,g1) = 0.2
FEATURE [PartDesign::Revolution] Revolution021
  AddSubType = 0
  Angle = 360
  Axis = (1e-16,1,-1e-16)
  Base = (0,0,0)
  ClaimChildren = false
  Fit = 0
  FitJoin = 0
  FixShape = 1
  InnerFit = 0
  InnerFitJoin = 0
  InvalidShape = false
  Linearize = true
  NewSolid = false
  Profile = -> Sketch205
  ReferenceAxis = -> Y_Axis120
  Refine = true
  Suppress = false
  TreeRank = 399
  ValidateShape = false
  _ProfileBasedVersion = 1
FEATURE [PartDesign::Body] Body100  label="V623ZZ-intern"
  AutoGroupSolids = false
  ClaimAllChildren = false
  ExportMode = 0
  FixShape = 1
  Group = -> [Sketch205,Revolution021]
  InvalidShape = false
  Origin = -> Origin193
  SingleSolid = true
  Tip = -> Revolution021
  TreeRank = 385
  ValidateShape = false
  _ExportChildren = -> [Revolution021]
  _GroupVersion = 1
COMPONENT P23 — recipe-attached ("23HS16_0884S_equiped", modeled in this document).
Construction recipe (the document's own serialized feature program — sketch geometry with constraints, then the solid features built on it; lengths are millimeters unless a unit is written):

FEATURE [Sketcher::SketchObject] Sketch007
  ArcFitTolerance = 0
  AttachmentSupport = -> [XZ_Plane007]
  ExternalBSplineMaxDegree = 0
  ExternalBSplineTolerance = 0
  FixShape = 1
  FullyConstrained = true
  InternalTolerance = 1e-06
  InvalidShape = false
  MakeInternals = false
  MapMode = 5
  Placement = pos=(0,0,0) rot=(1,0,0;1.5708rad)
  Support = -> [XZ_Plane007]
  TreeRank = 0
  ValidateShape = false
  sketch-geometry (5):
    g0: LineSegment StartX=28.5 StartY=28.5 StartZ=0 EndX=-28.5 EndY=28.5 EndZ=0
    g1: LineSegment StartX=-28.5 StartY=28.5 StartZ=0 EndX=-28.5 EndY=-28.5 EndZ=0
    g2: LineSegment StartX=-28.5 StartY=-28.5 StartZ=0 EndX=28.5 EndY=-28.5 EndZ=0
    g3: LineSegment StartX=28.5 StartY=-28.5 StartZ=0 EndX=28.5 EndY=28.5 EndZ=0
    g4: Circle [constr] CenterX=2.6926e-12 CenterY=-1.717e-13 CenterZ=0 NormalX=0 NormalY=0 NormalZ=1 AngleXU=0 Radius=40.3051
  constraints (14):
    c: Coincident(g0,g1)
    c: Coincident(g1,g2)
    c: Coincident(g2,g3)
    c: Coincident(g3,g0)
    c: Equal(g0,g1)
    c: Equal(g0,g2)
    c: Equal(g0,g3)
    c: PointOnObject(g0,g4)
    c: PointOnObject(g1,g4)
    c: PointOnObject(g2,g4)
    c: PointOnObject(g3,g4)
    c: Coincident(g4,g-1)
    c: Horizontal(g0)
    c: DistanceX(g0,g0) = 57
FEATURE [PartDesign::Pad] Pad005
  AddSubType = 0
  AutoTaperInnerAngle = false
  CheckUpToFaceLimits = true
  ClaimChildren = false
  Direction = (1,1,1)
  Fit = 0
  FitJoin = 0
  FixShape = 1
  InnerFit = 0
  InnerFitJoin = 0
  InvalidShape = false
  Length = 11
  Length2 = 100
  NewSolid = false
  Placement = pos=(0,0,0) rot=(1,0,0;1.5708rad)
  Profile = -> Sketch007
  Refine = true
  Reversed = true
  Suppress = false
  TaperInnerAngle = 0
  TaperInnerAngleRev = 0
  TreeRank = 0
  Type = 0
  UsePipeForDraft = true
  ValidateShape = false
  _ProfileBasedVersion = 0
FEATURE [Sketcher::SketchObject] Sketch008
  ArcFitTolerance = 0
  AttachmentSupport = -> [Pad005]
  ExternalBSplineMaxDegree = 0
  ExternalBSplineTolerance = 0
  ExternalGeometry = -> [Pad005]
  FixShape = 1
  FullyConstrained = true
  InternalTolerance = 1e-06
  InvalidShape = false
  MakeInternals = false
  MapMode = 5
  Placement = pos=(0,11,2.4e-15) rot=(-1,0,0;1.5708rad)
  Support = -> [Pad005]
  TreeRank = 0
  ValidateShape = false
  sketch-geometry (5):
    g0: LineSegment StartX=-28.5 StartY=28.5 StartZ=0 EndX=-28.5 EndY=19.5 EndZ=0
    g1: LineSegment StartX=-28.5 StartY=19.5 StartZ=0 EndX=-23.5 EndY=19.5 EndZ=0
    g2: LineSegment StartX=-28.5 StartY=28.5 StartZ=0 EndX=-19.5 EndY=28.5 EndZ=0
    g3: LineSegment StartX=-19.5 StartY=28.5 StartZ=0 EndX=-19.5 EndY=23.5 EndZ=0
    g4: ArcOfCircle CenterX=-23.5 CenterY=23.5 CenterZ=0 NormalX=0 NormalY=0 NormalZ=1 AngleXU=0 Radius=4 StartAngle=4.71239 EndAngle=6.28319
  constraints (13):
    c: Vertical(g0)
    c: Coincident(g1,g0)
    c: Horizontal(g1)
    c: Coincident(g2,g0)
    c: Coincident(g3,g2)
    c: Vertical(g3)
    c: Horizontal(g2)
    c: Coincident(g0,g-4)
    c: Equal(g2,g0)
    c: Tangent(g4,g3) = 1.5708
    c: Tangent(g4,g1) = -1.5708
    c: DistanceY(g0,g0) = 9
    c: DistanceX(g4) = -23.5
FEATURE [PartDesign::Pocket] Pocket002
  AddSubType = 1
  AutoTaperInnerAngle = false
  BaseFeature = -> Pad005
  CheckUpToFaceLimits = true
  ClaimChildren = false
  Direction = (1,1,1)
  Fit = 0
  FitJoin = 0
  FixShape = 1
  InnerFit = 0
  InnerFitJoin = 0
  InvalidShape = false
  Length = 5
  Length2 = 100
  NewSolid = false
  Placement = pos=(0,0,0) rot=(1,0,0;1.5708rad)
  Profile = -> Sketch008
  Refine = true
  Suppress = false
  TaperInnerAngle = 0
  TaperInnerAngleRev = 0
  TreeRank = 0
  Type = 0
  ValidateShape = false
  _ProfileBasedVersion = 0
  _Version = 0
FEATURE [PartDesign::PolarPattern] PolarPattern007
  AddSubType = 0
  Angle = 360
  Axis = -> Sketch008 [N_Axis]
  BaseFeature = -> Pocket002
  CopyShape = false
  FixShape = 1
  InvalidShape = false
  NewSolid = false
  Occurrences = 4
  OriginalSubs = -> [Pocket002]
  Originals = -> [Pocket002]
  ParallelTransform = true
  Placement = pos=(0,0,0) rot=(1,0,0;1.5708rad)
  Refine = true
  SubTransform = true
  Suppress = false
  TreeRank = 0
  ValidateShape = false
  _Version = 0
FEATURE [Sketcher::SketchObject] Sketch009
  ArcFitTolerance = 0
  AttachmentSupport = -> [XZ_Plane007]
  ExternalBSplineMaxDegree = 0
  ExternalBSplineTolerance = 0
  FixShape = 1
  FullyConstrained = true
  InternalTolerance = 1e-06
  InvalidShape = false
  MakeInternals = false
  MapMode = 5
  Placement = pos=(0,0,0) rot=(1,0,0;1.5708rad)
  Support = -> [XZ_Plane007]
  TreeRank = 0
  ValidateShape = false
  sketch-geometry (2):
    g0: Circle CenterX=23.5 CenterY=23.5 CenterZ=0 NormalX=0 NormalY=0 NormalZ=1 AngleXU=0 Radius=2.55
    g1: LineSegment [constr] StartX=-1.146e-13 StartY=5.53e-14 StartZ=0 EndX=23.5 EndY=23.5 EndZ=0
  constraints (5):
    c: DistanceX(g0) = 23.5
    c: Coincident(g1,g-1)
    c: Coincident(g1,g0)
    c: Angle(g-1,g1) = 0.785398
    c: Diameter(g0) = 5.1
FEATURE [PartDesign::Pocket] Pocket003
  AddSubType = 1
  AutoTaperInnerAngle = false
  BaseFeature = -> PolarPattern007
  CheckUpToFaceLimits = true
  ClaimChildren = false
  Direction = (1,1,1)
  Fit = 0
  FitJoin = 0
  FixShape = 1
  InnerFit = 0
  InnerFitJoin = 0
  InvalidShape = false
  Length = 5
  Length2 = 100
  NewSolid = false
  Placement = pos=(0,0,0) rot=(1,0,0;1.5708rad)
  Profile = -> Sketch009
  Refine = true
  Suppress = false
  TaperInnerAngle = 0
  TaperInnerAngleRev = 0
  TreeRank = 0
  Type = 1
  ValidateShape = false
  _ProfileBasedVersion = 0
  _Version = 0
FEATURE [PartDesign::PolarPattern] PolarPattern008
  AddSubType = 0
  Angle = 360
  Axis = -> Sketch009 [N_Axis]
  BaseFeature = -> Pocket003
  CopyShape = false
  FixShape = 1
  InvalidShape = false
  NewSolid = false
  Occurrences = 4
  OriginalSubs = -> [Pocket003]
  Originals = -> [Pocket003]
  ParallelTransform = true
  Placement = pos=(0,0,0) rot=(1,0,0;1.5708rad)
  Refine = true
  SubTransform = true
  Suppress = false
  TreeRank = 0
  ValidateShape = false
  _Version = 0
FEATURE [Sketcher::SketchObject] Sketch010
  ArcFitTolerance = 0
  AttachmentSupport = -> [XZ_Plane007]
  ExternalBSplineMaxDegree = 0
  ExternalBSplineTolerance = 0
  FixShape = 1
  FullyConstrained = true
  InternalTolerance = 1e-06
  InvalidShape = false
  MakeInternals = false
  MapMode = 5
  Placement = pos=(0,0,0) rot=(1,0,0;1.5708rad)
  Support = -> [XZ_Plane007]
  TreeRank = 0
  ValidateShape = false
  sketch-geometry (1):
    g0: Circle CenterX=0 CenterY=0 CenterZ=0 NormalX=0 NormalY=0 NormalZ=1 AngleXU=0 Radius=19
  constraints (2):
    c: Coincident(g0,g-1)
    c: Diameter(g0) = 38
FEATURE [PartDesign::Pad] Pad006
  AddSubType = 0
  AutoTaperInnerAngle = false
  BaseFeature = -> PolarPattern008
  CheckUpToFaceLimits = true
  ClaimChildren = false
  Direction = (1,1,1)
  Fit = 0
  FitJoin = 0
  FixShape = 1
  InnerFit = 0
  InnerFitJoin = 0
  InvalidShape = false
  Length = 1.6
  Length2 = 100
  NewSolid = false
  Placement = pos=(0,0,0) rot=(1,0,0;1.5708rad)
  Profile = -> Sketch010
  Refine = true
  Suppress = false
  TaperInnerAngle = 0
  TaperInnerAngleRev = 0
  TreeRank = 0
  Type = 0
  UsePipeForDraft = true
  ValidateShape = false
  _ProfileBasedVersion = 0
FEATURE [Sketcher::SketchObject] Sketch011
  ArcFitTolerance = 0
  AttachmentSupport = -> [XZ_Plane007]
  ExternalBSplineMaxDegree = 0
  ExternalBSplineTolerance = 0
  FixShape = 1
  FullyConstrained = true
  InternalTolerance = 1e-06
  InvalidShape = false
  MakeInternals = false
  MapMode = 5
  Placement = pos=(0,0,0) rot=(1,0,0;1.5708rad)
  Support = -> [XZ_Plane007]
  TreeRank = 0
  ValidateShape = false
  sketch-geometry (1):
    g0: Circle CenterX=0 CenterY=0 CenterZ=0 NormalX=0 NormalY=0 NormalZ=1 AngleXU=0 Radius=5
  constraints (2):
    c: Coincident(g0,g-1)
    c: Diameter(g0) = 10
FEATURE [PartDesign::Pocket] Pocket004
  AddSubType = 1
  AutoTaperInnerAngle = false
  BaseFeature = -> Pad006
  CheckUpToFaceLimits = true
  ClaimChildren = false
  Direction = (1,1,1)
  Fit = 0
  FitJoin = 0
  FixShape = 1
  InnerFit = 0
  InnerFitJoin = 0
  InvalidShape = false
  Length = 5
  Length2 = 100
  NewSolid = false
  Placement = pos=(0,0,0) rot=(1,0,0;1.5708rad)
  Profile = -> Sketch011
  Refine = true
  Reversed = true
  Suppress = false
  TaperInnerAngle = 0
  TaperInnerAngleRev = 0
  TreeRank = 0
  Type = 1
  ValidateShape = false
  _ProfileBasedVersion = 0
  _Version = 0
FEATURE [PartDesign::Fillet] Fillet
  AddSubType = 0
  Base = -> Pocket004 [Edge2,Edge8,Edge51,Edge17]
  BaseFeature = -> Pocket004
  FixShape = 1
  InvalidShape = false
  NewSolid = false
  Placement = pos=(0,0,0) rot=(1,0,0;1.5708rad)
  Radius = 3
  Refine = true
  SupportTransform = false
  Suppress = false
  TreeRank = 0
  UseAllEdges = false
  ValidateShape = false
FEATURE [Sketcher::SketchObject] Sketch012
  ArcFitTolerance = 0
  AttachmentSupport = -> [XZ_Plane007]
  ExternalBSplineMaxDegree = 0
  ExternalBSplineTolerance = 0
  ExternalGeometry = -> [Fillet]
  FixShape = 1
  FullyConstrained = true
  InternalTolerance = 1e-06
  InvalidShape = false
  MakeInternals = false
  MapMode = 5
  Placement = pos=(0,0,0) rot=(1,0,0;1.5708rad)
  Support = -> [XZ_Plane007]
  TreeRank = 0
  ValidateShape = false
  sketch-geometry (5):
    g0: ArcOfCircle CenterX=16.4 CenterY=28.5 CenterZ=0 NormalX=0 NormalY=0 NormalZ=1 AngleXU=0 Radius=3.1 StartAngle=0 EndAngle=3.14159
    g1: ArcOfCircle CenterX=16.4 CenterY=25.4 CenterZ=0 NormalX=0 NormalY=0 NormalZ=1 AngleXU=0 Radius=3.1 StartAngle=3.14159 EndAngle=6.28319
    g2: LineSegment StartX=13.3 StartY=28.5 StartZ=0 EndX=13.3 EndY=25.4 EndZ=0
    g3: LineSegment StartX=19.5 StartY=28.5 StartZ=0 EndX=19.5 EndY=25.4 EndZ=0
    g4: Circle [constr] CenterX=16.4 CenterY=25.4 CenterZ=0 NormalX=0 NormalY=0 NormalZ=1 AngleXU=0 Radius=3.1
  constraints (12):
    c: Tangent(g0,g3) = 1.5708
    c: Tangent(g0,g2) = -1.5708
    c: Tangent(g2,g1) = -1.5708
    c: Tangent(g3,g1) = 1.5708
    c: Vertical(g2)
    c: Equal(g0,g1)
    c: PointOnObject(g0,g-3)
    c: Coincident(g4,g1)
    c: PointOnObject(g1,g4)
    c: PointOnObject(g0,g4)
    c: Diameter(g1) = 6.2
    c: DistanceX(g-1,g1) = 16.4
FEATURE [PartDesign::Pocket] Pocket005
  AddSubType = 1
  AutoTaperInnerAngle = false
  BaseFeature = -> Fillet
  CheckUpToFaceLimits = true
  ClaimChildren = false
  Direction = (1,1,1)
  Fit = 0
  FitJoin = 0
  FixShape = 1
  InnerFit = 0
  InnerFitJoin = 0
  InvalidShape = false
  Length = 2.5
  Length2 = 100
  NewSolid = false
  Placement = pos=(0,0,0) rot=(1,0,0;1.5708rad)
  Profile = -> Sketch012
  Refine = true
  Suppress = false
  TaperInnerAngle = 0
  TaperInnerAngleRev = 0
  TreeRank = 0
  Type = 0
  ValidateShape = false
  _ProfileBasedVersion = 0
  _Version = 0
FEATURE [PartDesign::PolarPattern] PolarPattern009
  AddSubType = 0
  Angle = 360
  Axis = -> Sketch012 [N_Axis]
  BaseFeature = -> Pocket005
  CopyShape = false
  FixShape = 1
  InvalidShape = false
  NewSolid = false
  Occurrences = 4
  OriginalSubs = -> [Pocket005]
  Originals = -> [Pocket005]
  ParallelTransform = true
  Placement = pos=(0,0,0) rot=(1,0,0;1.5708rad)
  Refine = true
  SubTransform = true
  Suppress = false
  TreeRank = 0
  ValidateShape = false
  _Version = 0
FEATURE [Sketcher::SketchObject] Sketch013
  ArcFitTolerance = 0
  AttachmentSupport = -> [XZ_Plane007]
  ExternalBSplineMaxDegree = 0
  ExternalBSplineTolerance = 0
  ExternalGeometry = -> [PolarPattern009]
  FixShape = 1
  FullyConstrained = true
  InternalTolerance = 1e-06
  InvalidShape = false
  MakeInternals = false
  MapMode = 5
  Placement = pos=(0,0,0) rot=(1,0,0;1.5708rad)
  Support = -> [XZ_Plane007]
  TreeRank = 0
  ValidateShape = false
  sketch-geometry (1):
    g0: Circle CenterX=16.4 CenterY=25.4 CenterZ=0 NormalX=0 NormalY=0 NormalZ=1 AngleXU=0 Radius=1.6
  constraints (2):
    c: Coincident(g0,g-3)
    c: Diameter(g0) = 3.2
FEATURE [PartDesign::Pocket] Pocket006
  AddSubType = 1
  AutoTaperInnerAngle = false
  BaseFeature = -> PolarPattern009
  CheckUpToFaceLimits = true
  ClaimChildren = false
  Direction = (1,1,1)
  Fit = 0
  FitJoin = 0
  FixShape = 1
  InnerFit = 0
  InnerFitJoin = 0
  InvalidShape = false
  Length = 5
  Length2 = 100
  NewSolid = false
  Placement = pos=(0,0,0) rot=(1,0,0;1.5708rad)
  Profile = -> Sketch013
  Refine = true
  Suppress = false
  TaperInnerAngle = 0
  TaperInnerAngleRev = 0
  TreeRank = 0
  Type = 1
  ValidateShape = false
  _ProfileBasedVersion = 0
  _Version = 0
FEATURE [PartDesign::PolarPattern] PolarPattern010
  AddSubType = 0
  Angle = 360
  Axis = -> Sketch013 [N_Axis]
  BaseFeature = -> Pocket006
  CopyShape = false
  FixShape = 1
  InvalidShape = false
  NewSolid = false
  Occurrences = 4
  OriginalSubs = -> [Pocket006]
  Originals = -> [Pocket006]
  ParallelTransform = true
  Placement = pos=(0,0,0) rot=(1,0,0;1.5708rad)
  Refine = true
  SubTransform = true
  Suppress = false
  TreeRank = 0
  ValidateShape = false
  _Version = 0
FEATURE [PartDesign::Fillet] Fillet001
  AddSubType = 0
  Base = -> PolarPattern010 [Edge10,Edge113,Edge8,Edge87,Edge114,Edge100,Edge86,Edge101,Edge97,Edge95,Edge81,Edge83,Edge2,Edge4,Edge110,Edge112]
  BaseFeature = -> PolarPattern010
  FixShape = 1
  InvalidShape = false
  NewSolid = false
  Placement = pos=(0,0,0) rot=(1,0,0;1.5708rad)
  Radius = 3
  Refine = true
  SupportTransform = false
  Suppress = false
  TreeRank = 0
  UseAllEdges = false
  ValidateShape = false
FEATURE [PartDesign::Body] Core  label="FrontPanel"
  AutoGroupSolids = false
  ClaimAllChildren = false
  ExportMode = 0
  FixShape = 1
  Group = -> [Sketch007,Pad005,Sketch008,Pocket002,PolarPattern007,Sketch009,Pocket003,PolarPattern008,Sketch010,Pad006,Sketch011,Pocket004,Fillet,Sketch012,Pocket005,PolarPattern009,Sketch013,Pocket006,PolarPattern010,Fillet001]
  InvalidShape = false
  Origin = -> Origin010
  SingleSolid = true
  Tip = -> Fillet001
  TreeRank = 0
  ValidateShape = false
  _ExportChildren = -> [Pad005,Pocket002,PolarPattern007,Pocket003,PolarPattern008,Pad006,Pocket004,Fillet,Pocket005,PolarPattern009,Pocket006,PolarPattern010,Fillet001]
  _GroupVersion = 1
FEATURE [PartDesign::ShapeBinder] ShapeBinder
  FixShape = 1
  InvalidShape = false
  Placement = pos=(0,0,0) rot=(1,0,0;1.5708rad)
  Support = -> [Fillet001]
  TraceSupport = false
  TreeRank = 0
  ValidateShape = false
FEATURE [PartDesign::Pad] Pad007
  AddSubType = 0
  AutoTaperInnerAngle = false
  CheckUpToFaceLimits = true
  ClaimChildren = false
  Direction = (1,1,1)
  Fit = 0
  FitJoin = 0
  FixShape = 1
  InnerFit = 0
  InnerFitJoin = 0
  InvalidShape = false
  Length = 20
  Length2 = 100
  NewSolid = false
  Placement = pos=(0,0,0) rot=(1,0,0;1.5708rad)
  Profile = -> ShapeBinder
  Refine = true
  Suppress = false
  TaperInnerAngle = 0
  TaperInnerAngleRev = 0
  TreeRank = 0
  Type = 0
  UsePipeForDraft = true
  ValidateShape = false
  _ProfileBasedVersion = 0
FEATURE [PartDesign::Body] Body006  label="MiddleCore"
  AutoGroupSolids = false
  ClaimAllChildren = false
  ExportMode = 0
  FixShape = 1
  Group = -> [ShapeBinder,Pad007]
  InvalidShape = false
  Origin = -> Origin011
  SingleSolid = true
  Tip = -> Pad007
  TreeRank = 0
  ValidateShape = false
  _ExportChildren = -> [Pad007]
  _GroupVersion = 1
FEATURE [PartDesign::ShapeBinder] ShapeBinder001
  FixShape = 1
  InvalidShape = false
  Placement = pos=(0,20,4.4e-15) rot=(1,0,0;1.5708rad)
  Support = -> [Pad007]
  TraceSupport = false
  TreeRank = 0
  ValidateShape = false
FEATURE [PartDesign::Pad] Pad008
  AddSubType = 0
  AutoTaperInnerAngle = false
  CheckUpToFaceLimits = true
  ClaimChildren = false
  Direction = (1,1,1)
  Fit = 0
  FitJoin = 0
  FixShape = 1
  InnerFit = 0
  InnerFitJoin = 0
  InvalidShape = false
  Length = 11
  Length2 = 100
  NewSolid = false
  Placement = pos=(0,20,4.4e-15) rot=(1,0,0;1.5708rad)
  Profile = -> ShapeBinder001
  Refine = true
  Suppress = false
  TaperInnerAngle = 0
  TaperInnerAngleRev = 0
  TreeRank = 0
  Type = 0
  UsePipeForDraft = true
  ValidateShape = false
  _ProfileBasedVersion = 0
FEATURE [Sketcher::SketchObject] Sketch014
  ArcFitTolerance = 0
  AttachmentSupport = -> [XZ_Plane009]
  ExternalBSplineMaxDegree = 0
  ExternalBSplineTolerance = 0
  FixShape = 1
  FullyConstrained = true
  InternalTolerance = 1e-06
  InvalidShape = false
  MakeInternals = false
  MapMode = 5
  Placement = pos=(0,0,0) rot=(1,0,0;1.5708rad)
  Support = -> [XZ_Plane009]
  TreeRank = 0
  ValidateShape = false
  sketch-geometry (1):
    g0: Circle CenterX=0 CenterY=0 CenterZ=0 NormalX=0 NormalY=0 NormalZ=1 AngleXU=0 Radius=5
  constraints (2):
    c: Coincident(g0,g-1)
    c: Diameter(g0) = 10
FEATURE [PartDesign::Pocket] Pocket007
  AddSubType = 1
  AutoTaperInnerAngle = false
  BaseFeature = -> Pad008
  CheckUpToFaceLimits = true
  ClaimChildren = false
  Direction = (1,1,1)
  Fit = 0
  FitJoin = 0
  FixShape = 1
  InnerFit = 0
  InnerFitJoin = 0
  InvalidShape = false
  Length = 5
  Length2 = 100
  NewSolid = false
  Placement = pos=(0,20,4.4e-15) rot=(1,0,0;1.5708rad)
  Profile = -> Sketch014
  Refine = true
  Suppress = false
  TaperInnerAngle = 0
  TaperInnerAngleRev = 0
  TreeRank = 0
  Type = 1
  ValidateShape = false
  _ProfileBasedVersion = 0
  _Version = 0
FEATURE [PartDesign::Fillet] Fillet002
  AddSubType = 0
  Base = -> Pocket007 [Edge51,Edge61]
  BaseFeature = -> Pocket007
  FixShape = 1
  InvalidShape = false
  NewSolid = false
  Placement = pos=(0,20,4.4e-15) rot=(1,0,0;1.5708rad)
  Radius = 0.5
  Refine = true
  SupportTransform = false
  Suppress = false
  TreeRank = 0
  UseAllEdges = false
  ValidateShape = false
FEATURE [PartDesign::Body] Body007  label="RearPanel"
  AutoGroupSolids = false
  ClaimAllChildren = false
  ExportMode = 0
  FixShape = 1
  Group = -> [ShapeBinder001,Pad008,Sketch014,Pocket007,Fillet002]
  InvalidShape = false
  Origin = -> Origin012
  SingleSolid = true
  Tip = -> Fillet002
  TreeRank = 0
  ValidateShape = false
  _ExportChildren = -> [Pad008,Pocket007,Fillet002]
  _GroupVersion = 1
FEATURE [Sketcher::SketchObject] Sketch015
  ArcFitTolerance = 0
  AttachmentSupport = -> [XZ_Plane010]
  ExternalBSplineMaxDegree = 0
  ExternalBSplineTolerance = 0
  FixShape = 1
  FullyConstrained = true
  InternalTolerance = 1e-06
  InvalidShape = false
  MakeInternals = false
  MapMode = 5
  Placement = pos=(0,0,0) rot=(1,0,0;1.5708rad)
  Support = -> [XZ_Plane010]
  TreeRank = 0
  ValidateShape = false
  sketch-geometry (1):
    g0: Circle CenterX=0 CenterY=0 CenterZ=0 NormalX=0 NormalY=0 NormalZ=1 AngleXU=0 Radius=3.175
  constraints (2):
    c: Coincident(g0,g-1)
    c: Diameter(g0) = 6.35
FEATURE [PartDesign::Pad] Pad009
  AddSubType = 0
  AutoTaperInnerAngle = false
  CheckUpToFaceLimits = true
  ClaimChildren = false
  Direction = (1,1,1)
  Fit = 0
  FitJoin = 0
  FixShape = 1
  InnerFit = 0
  InnerFitJoin = 0
  InvalidShape = false
  Length = 20.6
  Length2 = 100
  NewSolid = false
  Placement = pos=(0,0,0) rot=(1,0,0;1.5708rad)
  Profile = -> Sketch015
  Refine = true
  Suppress = false
  TaperInnerAngle = 0
  TaperInnerAngleRev = 0
  TreeRank = 0
  Type = 0
  UsePipeForDraft = true
  ValidateShape = false
  _ProfileBasedVersion = 0
FEATURE [Sketcher::SketchObject] Sketch016
  ArcFitTolerance = 0
  AttachmentSupport = -> [XY_Plane010]
  ExternalBSplineMaxDegree = 0
  ExternalBSplineTolerance = 0
  ExternalGeometry = -> [Pad009]
  FixShape = 1
  FullyConstrained = true
  InternalTolerance = 1e-06
  InvalidShape = false
  MakeInternals = false
  MapMode = 5
  Support = -> [XY_Plane010]
  TreeRank = 0
  ValidateShape = false
  sketch-geometry (4):
    g0: LineSegment StartX=3.175 StartY=-20.6 StartZ=0 EndX=2.675 EndY=-20.6 EndZ=0
    g1: LineSegment StartX=2.675 StartY=-20.6 StartZ=0 EndX=2.675 EndY=-5.6 EndZ=0
    g2: LineSegment StartX=2.675 StartY=-5.6 StartZ=0 EndX=3.175 EndY=-5.6 EndZ=0
    g3: LineSegment StartX=3.175 StartY=-5.6 StartZ=0 EndX=3.175 EndY=-20.6 EndZ=0
  constraints (11):
    c: Coincident(g0,g1)
    c: Coincident(g1,g2)
    c: Coincident(g2,g3)
    c: Coincident(g3,g0)
    c: Horizontal(g0)
    c: Horizontal(g2)
    c: Vertical(g1)
    c: Vertical(g3)
    c: Coincident(g0,g-3)
    c: DistanceX(g-3,g0) = 5.85
    c: DistanceY(g3,g3) = 15
FEATURE [PartDesign::Pocket] Pocket008
  AddSubType = 1
  AutoTaperInnerAngle = false
  BaseFeature = -> Pad009
  CheckUpToFaceLimits = true
  ClaimChildren = false
  Direction = (1,1,1)
  Fit = 0
  FitJoin = 0
  FixShape = 1
  InnerFit = 0
  InnerFitJoin = 0
  InvalidShape = false
  Length = 5
  Length2 = 100
  Midplane = true
  NewSolid = false
  Placement = pos=(0,0,0) rot=(1,0,0;1.5708rad)
  Profile = -> Sketch016
  Refine = true
  Suppress = false
  TaperInnerAngle = 0
  TaperInnerAngleRev = 0
  TreeRank = 0
  Type = 1
  ValidateShape = false
  _ProfileBasedVersion = 0
  _Version = 0
FEATURE [PartDesign::Chamfer] Chamfer
  AddSubType = 0
  Angle = 45
  Base = -> Pocket008 [Edge5]
  BaseFeature = -> Pocket008
  ChamferType = 0
  FixShape = 1
  FlipDirection = false
  InvalidShape = false
  NewSolid = false
  Placement = pos=(0,0,0) rot=(1,0,0;1.5708rad)
  Refine = true
  Size = 0.4
  Size2 = 1
  SupportTransform = false
  Suppress = false
  TreeRank = 0
  UseAllEdges = false
  ValidateShape = false
FEATURE [PartDesign::Body] Body008  label="Axle"
  AutoGroupSolids = false
  ClaimAllChildren = false
  ExportMode = 0
  FixShape = 1
  Group = -> [Sketch015,Pad009,Sketch016,Pocket008,Chamfer]
  InvalidShape = false
  Origin = -> Origin013
  SingleSolid = true
  Tip = -> Chamfer
  TreeRank = 0
  ValidateShape = false
  _ExportChildren = -> [Pad009,Pocket008,Chamfer]
  _GroupVersion = 1
FEATURE [PartDesign::ShapeBinder] ShapeBinder002
  FixShape = 1
  InvalidShape = false
  Placement = pos=(0,20,4.4e-15) rot=(1,0,0;1.5708rad)
  Support = -> [Fillet002]
  TraceSupport = false
  TreeRank = 0
  ValidateShape = false
FEATURE [Sketcher::SketchObject] Sketch017
  ArcFitTolerance = 0
  AttachmentSupport = -> [ShapeBinder002]
  ExternalBSplineMaxDegree = 0
  ExternalBSplineTolerance = 0
  ExternalGeometry = -> [ShapeBinder002]
  FixShape = 1
  FullyConstrained = true
  InternalTolerance = 1e-06
  InvalidShape = false
  MakeInternals = false
  MapMode = 5
  Placement = pos=(-2.7551e-12,20,-28.5) rot=(1,0,0;3.14159rad)
  Support = -> [ShapeBinder002]
  TreeRank = 0
  ValidateShape = false
  sketch-geometry (5):
    g0: LineSegment StartX=-6 StartY=-11 StartZ=0 EndX=6 EndY=-11 EndZ=0
    g1: LineSegment StartX=6 StartY=-11 StartZ=0 EndX=6 EndY=-21.5 EndZ=0
    g2: LineSegment StartX=6 StartY=-21.5 StartZ=0 EndX=-6 EndY=-21.5 EndZ=0
    g3: LineSegment StartX=-6 StartY=-21.5 StartZ=0 EndX=-6 EndY=-11 EndZ=0
    g4: Circle CenterX=4.8501e-12 CenterY=-16.25 CenterZ=0 NormalX=0 NormalY=0 NormalZ=1 AngleXU=0 Radius=2.5
  constraints (13):
    c: Coincident(g0,g1)
    c: Coincident(g1,g2)
    c: Coincident(g2,g3)
    c: Coincident(g3,g0)
    c: Horizontal(g2)
    c: Vertical(g1)
    c: Vertical(g3)
    c: Symmetric(g0,g0,g-2)
    c: PointOnObject(g2,g-4)
    c: PointOnObject(g0,g-3)
    c: DistanceX(g2,g2) = 12
    c: Symmetric(g2,g0,g4)
    c: Diameter(g4) = 5
FEATURE [PartDesign::Pad] Pad010
  AddSubType = 0
  AutoTaperInnerAngle = false
  CheckUpToFaceLimits = true
  ClaimChildren = false
  Direction = (1,1,1)
  Fit = 0
  FitJoin = 0
  FixShape = 1
  InnerFit = 0
  InnerFitJoin = 0
  InvalidShape = false
  Length = 0.8
  Length2 = 100
  NewSolid = false
  Placement = pos=(0,20,4.4e-15) rot=(1,0,0;1.5708rad)
  Profile = -> Sketch017
  Refine = true
  Suppress = false
  TaperInnerAngle = 0
  TaperInnerAngleRev = 0
  TreeRank = 0
  Type = 0
  UsePipeForDraft = true
  ValidateShape = false
  _ProfileBasedVersion = 0
FEATURE [PartDesign::Fillet] Fillet003
  AddSubType = 0
  Base = -> Pad010 [Edge5,Edge2,Edge8,Edge1]
  BaseFeature = -> Pad010
  FixShape = 1
  InvalidShape = false
  NewSolid = false
  Placement = pos=(0,20,4.4e-15) rot=(1,0,0;1.5708rad)
  Radius = 1
  Refine = true
  SupportTransform = false
  Suppress = false
  TreeRank = 0
  UseAllEdges = false
  ValidateShape = false
FEATURE [PartDesign::Body] Body009  label="ProtectCable"
  AutoGroupSolids = false
  ClaimAllChildren = false
  ExportMode = 0
  FixShape = 1
  Group = -> [ShapeBinder002,Sketch017,Pad010,Fillet003]
  InvalidShape = false
  Origin = -> Origin014
  SingleSolid = true
  Tip = -> Fillet003
  TreeRank = 0
  ValidateShape = false
  _ExportChildren = -> [ShapeBinder002,Pad010,Fillet003]
  _GroupVersion = 1
FEATURE [PartDesign::ShapeBinder] ShapeBinder003
  FixShape = 1
  InvalidShape = false
  Support = -> [Fillet003]
  TraceSupport = false
  TreeRank = 0
  ValidateShape = false
FEATURE [Sketcher::SketchObject] Sketch018
  ArcFitTolerance = 0
  AttachmentSupport = -> [ShapeBinder003]
  ExternalBSplineMaxDegree = 0
  ExternalBSplineTolerance = 0
  ExternalGeometry = -> [ShapeBinder003]
  FixShape = 1
  FullyConstrained = true
  InternalTolerance = 1e-06
  InvalidShape = false
  MakeInternals = false
  MapMode = 5
  Placement = pos=(-2.7591e-12,9.4e-15,-28.5) rot=(0,0,1;0rad)
  Support = -> [ShapeBinder003]
  TreeRank = 0
  ValidateShape = false
  sketch-geometry (5):
    g0: Circle [constr] CenterX=4.9993e-12 CenterY=36.25 CenterZ=0 NormalX=0 NormalY=0 NormalZ=1 AngleXU=0 Radius=0.35
    g1: Circle CenterX=-6.77e-14 CenterY=37.5 CenterZ=0 NormalX=0 NormalY=0 NormalZ=1 AngleXU=0 Radius=0.9
    g2: Circle [constr] CenterX=1.25 CenterY=36.25 CenterZ=0 NormalX=0 NormalY=0 NormalZ=1 AngleXU=0 Radius=0.9
    g3: Circle [constr] CenterX=-1.25 CenterY=36.25 CenterZ=0 NormalX=0 NormalY=0 NormalZ=1 AngleXU=0 Radius=0.9
    g4: Circle [constr] CenterX=8.325e-13 CenterY=35 CenterZ=0 NormalX=0 NormalY=0 NormalZ=1 AngleXU=0 Radius=0.9
  constraints (13):
    c: Coincident(g0,g-3)
    c: PointOnObject(g1,g-2)
    c: Tangent(g1,g0)
    c: Tangent(g2,g0)
    c: Tangent(g3,g0)
    c: PointOnObject(g4,g-2)
    c: Tangent(g4,g0)
    c: Equal(g4,g2)
    c: Equal(g3,g1)
    c: Symmetric(g2,g3,g-3)
    c: Horizontal(g3,g2)
    c: Diameter(g1) = 1.8
    c: DistanceY(g-3,g1) = 1.25
FEATURE [PartDesign::Line] DatumLine
  AttacherType = Attacher::AttachEngineLine
  AttachmentSupport = -> [ShapeBinder003]
  FixShape = 1
  InvalidShape = false
  Length = 10
  MapMode = 19
  MinimumLength = 10
  Placement = pos=(2.0948e-12,36.25,-28.5) rot=(-1,0,0;3.14159rad)
  ResizeMode = 0
  Support = -> [ShapeBinder003]
  TreeRank = 0
  ValidateShape = false
FEATURE [PartDesign::Pad] Pad011
  AddSubType = 0
  AutoTaperInnerAngle = false
  CheckUpToFaceLimits = true
  ClaimChildren = false
  Direction = (1,1,1)
  Fit = 0
  FitJoin = 0
  FixShape = 1
  InnerFit = 0
  InnerFitJoin = 0
  InvalidShape = false
  Length = 5
  Length2 = 100
  NewSolid = false
  Profile = -> Sketch018
  Refine = true
  Reversed = true
  Suppress = false
  TaperInnerAngle = 0
  TaperInnerAngleRev = 0
  TreeRank = 0
  Type = 0
  UsePipeForDraft = true
  ValidateShape = false
  _ProfileBasedVersion = 0
FEATURE [PartDesign::PolarPattern] PolarPattern011
  AddSubType = 0
  Angle = 360
  Axis = -> DatumLine
  BaseFeature = -> Pad011
  CopyShape = false
  FixShape = 1
  InvalidShape = false
  NewSolid = false
  Occurrences = 4
  OriginalSubs = -> [Pad011]
  Originals = -> [Pad011]
  ParallelTransform = true
  Refine = true
  SubTransform = true
  Suppress = false
  TreeRank = 0
  ValidateShape = false
  _Version = 0
FEATURE [PartDesign::Body] Body010  label="Cables"
  AutoGroupSolids = false
  ClaimAllChildren = false
  ExportMode = 0
  FixShape = 1
  Group = -> [ShapeBinder003,Sketch018,DatumLine,Pad011,PolarPattern011]
  InvalidShape = false
  Origin = -> Origin006
  SingleSolid = true
  Tip = -> PolarPattern011
  TreeRank = 0
  ValidateShape = false
  _ExportChildren = -> [ShapeBinder003,DatumLine,Pad011,PolarPattern011]
  _GroupVersion = 1
FEATURE [Sketcher::SketchObject] Sketch020
  ArcFitTolerance = 0
  AttachmentSupport = -> [XY_Plane013]
  ExternalBSplineMaxDegree = 0
  ExternalBSplineTolerance = 0
  FixShape = 1
  FullyConstrained = true
  InternalTolerance = 1e-06
  InvalidShape = false
  MakeInternals = false
  MapMode = 5
  Support = -> [XY_Plane013]
  TreeRank = 0
  ValidateShape = false
  sketch-geometry (4):
    g0: LineSegment StartX=3 StartY=0 StartZ=0 EndX=12.5 EndY=0 EndZ=0
    g1: LineSegment StartX=12.5 StartY=0 StartZ=0 EndX=12.5 EndY=-15 EndZ=0
    g2: LineSegment StartX=12.5 StartY=-15 StartZ=0 EndX=3 EndY=-15 EndZ=0
    g3: LineSegment StartX=3 StartY=-15 StartZ=0 EndX=3 EndY=0 EndZ=0
  constraints (12):
    c: PointOnObject(g0,g-1)
    c: PointOnObject(g0,g-1)
    c: Vertical(g1)
    c: Coincident(g1,g2)
    c: Horizontal(g2)
    c: Coincident(g2,g3)
    c: Coincident(g3,g0)
    c: Vertical(g3)
    c: DistanceX(g0) = 3
    c: DistanceY(g2) = -15
    c: DistanceX(g1) = 12.5
    c: Coincident(g0,g1)
FEATURE [PartDesign::Revolution] Revolution
  AddSubType = 0
  Angle = 360
  Axis = (0,1,0)
  Base = (0,0,0)
  ClaimChildren = false
  Fit = 0
  FitJoin = 0
  FixShape = 1
  InnerFit = 0
  InnerFitJoin = 0
  InvalidShape = false
  NewSolid = false
  Profile = -> Sketch020
  ReferenceAxis = -> Sketch020 [V_Axis]
  Refine = true
  Reversed = true
  Suppress = false
  TreeRank = 0
  ValidateShape = false
  _ProfileBasedVersion = 0
FEATURE [PartDesign::Body] Body011  label="Poulie_T5_14T_10mm"
  AutoGroupSolids = false
  ClaimAllChildren = false
  ExportMode = 0
  FixShape = 1
  Group = -> [Sketch020,Revolution]
  InvalidShape = false
  Origin = -> Origin017
  Placement = pos=(0,-3,0) rot=(0,0,1;0rad)
  SingleSolid = true
  Tip = -> Revolution
  TreeRank = 0
  ValidateShape = false
  _ExportChildren = -> [Revolution]
  _GroupVersion = 1
PROVENANCE & LICENSES
A FreeCAD (.FCStd) document from a public repository crawl; recipes are the document's own serialized feature recipes (and, for linked parts, companion documents' recipes).
License: as declared in the source repository (recorded in the dataset sidecar).
